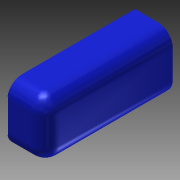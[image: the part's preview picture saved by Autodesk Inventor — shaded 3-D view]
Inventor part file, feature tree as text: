
AUTODESK INVENTOR PART (.ipt)
format: ipt  version: 2014 SP1 (Build 180222100, 222)  size: 183,296 bytes
history: native  units: in
note: dims shown in document units (in); Inventor stores cm internally (conversion verified against a paired STEP export)
features: reference x4, extrude x3, sketch x2, fillet x1, projected_geometry x1
ambient origin geometry x8: Origin, YZ Plane, XZ Plane, XY Plane, X Axis, Y Axis, Z Axis, Center Point
bodies: Solid1 (feature_tree)
feature tree (11):
  sketch  "Sketch1"  dims[d0=0.0625in d1=0.0in d3=1.0in]
  extrude  "Extrusion1"  Depth=1.0in
  extrude  "Extrusion2"  Depth=0.0625in
  extrude  "Extrusion3"  Depth=11.25in TaperAngle=0.0deg
  fillet  "Fillet1"  Radius=0.0625in
  reference  "Reference4"
  reference  "Reference5"
  sketch  "Sketch2"  dims[d7=1.0in d9=0.0625in d10=11.25in d11=0.0in d12=0.0625in d13=0.0in d14=1.3125in d15=0.0625in d16=0.0625in]
  reference  "Reference6"
  projected_geometry  "Projected Loop1"
  reference  "Reference7"
